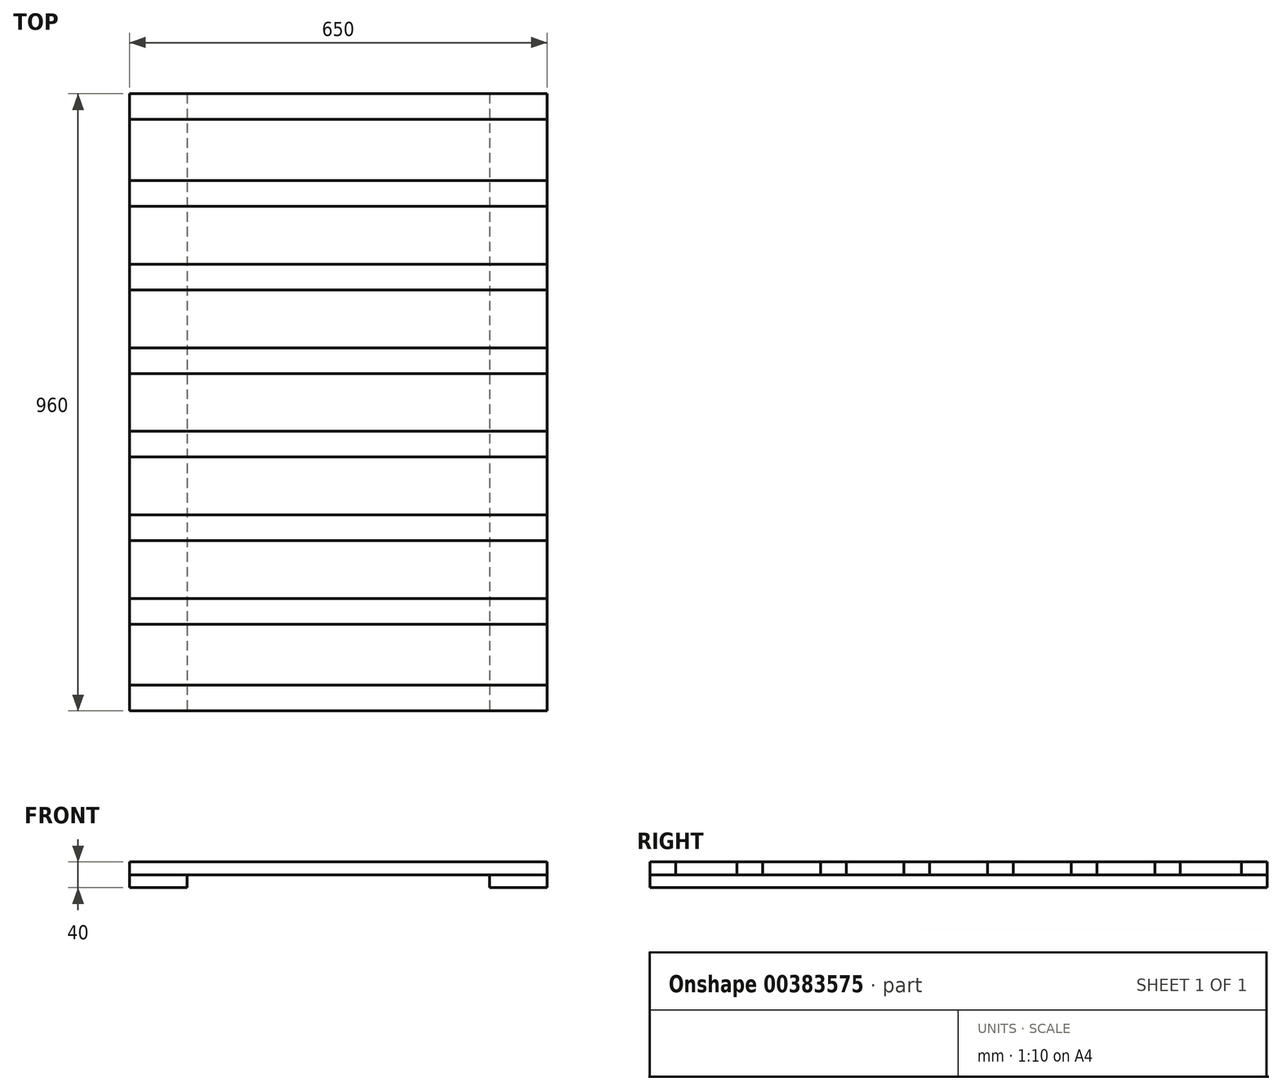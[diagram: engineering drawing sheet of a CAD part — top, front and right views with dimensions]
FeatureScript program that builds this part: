
annotation { "Feature Type Name" : "Feature", "Feature Type Description" : "" }
export const myFeature = defineFeature(function(context is Context, id is Id, definition is map)
    precondition{}
    {
        {
            var Q0;
            Q0=qCreatedBy(makeId("Top.planeOp"),FACE);
            var sketch = newSketch(context, id + "F0", { "sketchPlane" : qUnion([Q0])});
            skLineSegment(sketch, "E0.bottom", {"start": v(-273.15, 556.84) * mm, "end": v(376.85, 556.84) * mm});
            skLineSegment(sketch, "E0.top", {"start": v(-273.15, -403.16) * mm, "end": v(376.85, -403.16) * mm});
            skLineSegment(sketch, "E0.left", {"start": v(-273.15, 556.84) * mm, "end": v(-273.15, -403.16) * mm});
            skLineSegment(sketch, "E0.right", {"start": v(376.85, 556.84) * mm, "end": v(376.85, -403.16) * mm});
            skLineSegment(sketch, "E1", {"start": v(-273.15, 516.84) * mm, "end": v(376.85, 516.84) * mm});
            skLineSegment(sketch, "E2", {"start": v(-273.15, 421.84) * mm, "end": v(376.85, 421.84) * mm});
            skLineSegment(sketch, "E3", {"start": v(-273.15, 381.84) * mm, "end": v(376.85, 381.84) * mm});
            skLineSegment(sketch, "E4", {"start": v(-273.15, 291.84) * mm, "end": v(376.85, 291.84) * mm});
            skLineSegment(sketch, "E5", {"start": v(-273.15, 251.84) * mm, "end": v(376.85, 251.84) * mm});
            skLineSegment(sketch, "E6", {"start": v(-273.15, 161.84) * mm, "end": v(376.85, 161.84) * mm});
            skLineSegment(sketch, "E7", {"start": v(-273.15, 121.84) * mm, "end": v(376.85, 121.84) * mm});
            skLineSegment(sketch, "E8", {"start": v(-273.15, 31.84) * mm, "end": v(376.85, 31.84) * mm});
            skLineSegment(sketch, "E9", {"start": v(-273.15, -8.16) * mm, "end": v(376.85, -8.16) * mm});
            skLineSegment(sketch, "E10", {"start": v(-273.15, -98.16) * mm, "end": v(376.85, -98.16) * mm});
            skLineSegment(sketch, "E11", {"start": v(-273.15, -138.16) * mm, "end": v(376.85, -138.16) * mm});
            skLineSegment(sketch, "E12", {"start": v(-273.15, -228.16) * mm, "end": v(376.85, -228.16) * mm});
            skLineSegment(sketch, "E13", {"start": v(-273.15, -268.16) * mm, "end": v(376.85, -268.16) * mm});
            skLineSegment(sketch, "E14", {"start": v(-273.15, -363.16) * mm, "end": v(376.85, -363.16) * mm});
            skSolve(sketch);
        }
        {
            var Q0;
            {var subQ0=sQuery(id+"F0.wireOp",EDGE,"E0.bottom");Q0=makeQuery(id+"F0.imprint","IMPRINT",FACE,{"disambiguationData":[TD([[makeQuery(id+"F0.imprint","IMPRINT",EDGE,{"derivedFrom":subQ0}),-1.0]])]});}
            var Q1;
            {var subQ0=sQuery(id+"F0.wireOp",EDGE,"E2");Q1=makeQuery(id+"F0.imprint","IMPRINT",FACE,{"disambiguationData":[TD([[makeQuery(id+"F0.imprint","IMPRINT",EDGE,{"derivedFrom":subQ0}),-1.0]])]});}
            var Q2;
            {var subQ0=sQuery(id+"F0.wireOp",EDGE,"E4");Q2=makeQuery(id+"F0.imprint","IMPRINT",FACE,{"disambiguationData":[TD([[makeQuery(id+"F0.imprint","IMPRINT",EDGE,{"derivedFrom":subQ0}),-1.0]])]});}
            var Q3;
            {var subQ0=sQuery(id+"F0.wireOp",EDGE,"E6");Q3=makeQuery(id+"F0.imprint","IMPRINT",FACE,{"disambiguationData":[TD([[makeQuery(id+"F0.imprint","IMPRINT",EDGE,{"derivedFrom":subQ0}),-1.0]])]});}
            var Q4;
            {var subQ0=sQuery(id+"F0.wireOp",EDGE,"E8");Q4=makeQuery(id+"F0.imprint","IMPRINT",FACE,{"disambiguationData":[TD([[makeQuery(id+"F0.imprint","IMPRINT",EDGE,{"derivedFrom":subQ0}),-1.0]])]});}
            var Q5;
            {var subQ0=sQuery(id+"F0.wireOp",EDGE,"E10");Q5=makeQuery(id+"F0.imprint","IMPRINT",FACE,{"disambiguationData":[TD([[makeQuery(id+"F0.imprint","IMPRINT",EDGE,{"derivedFrom":subQ0}),-1.0]])]});}
            var Q6;
            {var subQ0=sQuery(id+"F0.wireOp",EDGE,"E12");Q6=makeQuery(id+"F0.imprint","IMPRINT",FACE,{"disambiguationData":[TD([[makeQuery(id+"F0.imprint","IMPRINT",EDGE,{"derivedFrom":subQ0}),-1.0]])]});}
            var Q7;
            {var subQ0=sQuery(id+"F0.wireOp",EDGE,"E0.top");Q7=makeQuery(id+"F0.imprint","IMPRINT",FACE,{"disambiguationData":[TD([[makeQuery(id+"F0.imprint","IMPRINT",EDGE,{"derivedFrom":subQ0}),1.0]])]});}
            extrude(context, id + "F1", {"entities" : qUnion([Q0, Q1, Q2, Q3, Q4, Q5, Q6, Q7]), "depth" : 20 * mm});
        }
        {
            var Q0;
            {var subQ0=sQuery(id+"F0.wireOp",EDGE,"E1");Q0=makeQuery(id+"F0.imprint","IMPRINT",FACE,{"disambiguationData":[TD([[makeQuery(id+"F0.imprint","IMPRINT",EDGE,{"derivedFrom":subQ0}),-1.0]])]});}
            var Q1;
            {var subQ0=sQuery(id+"F0.wireOp",EDGE,"E3");Q1=makeQuery(id+"F0.imprint","IMPRINT",FACE,{"disambiguationData":[TD([[makeQuery(id+"F0.imprint","IMPRINT",EDGE,{"derivedFrom":subQ0}),-1.0]])]});}
            var Q2;
            {var subQ0=sQuery(id+"F0.wireOp",EDGE,"E5");Q2=makeQuery(id+"F0.imprint","IMPRINT",FACE,{"disambiguationData":[TD([[makeQuery(id+"F0.imprint","IMPRINT",EDGE,{"derivedFrom":subQ0}),-1.0]])]});}
            var Q3;
            {var subQ0=sQuery(id+"F0.wireOp",EDGE,"E7");Q3=makeQuery(id+"F0.imprint","IMPRINT",FACE,{"disambiguationData":[TD([[makeQuery(id+"F0.imprint","IMPRINT",EDGE,{"derivedFrom":subQ0}),-1.0]])]});}
            var Q4;
            {var subQ0=sQuery(id+"F0.wireOp",EDGE,"E9");Q4=makeQuery(id+"F0.imprint","IMPRINT",FACE,{"disambiguationData":[TD([[makeQuery(id+"F0.imprint","IMPRINT",EDGE,{"derivedFrom":subQ0}),-1.0]])]});}
            var Q5;
            {var subQ0=sQuery(id+"F0.wireOp",EDGE,"E11");Q5=makeQuery(id+"F0.imprint","IMPRINT",FACE,{"disambiguationData":[TD([[makeQuery(id+"F0.imprint","IMPRINT",EDGE,{"derivedFrom":subQ0}),-1.0]])]});}
            var Q6;
            {var subQ0=sQuery(id+"F0.wireOp",EDGE,"E13");Q6=makeQuery(id+"F0.imprint","IMPRINT",FACE,{"disambiguationData":[TD([[makeQuery(id+"F0.imprint","IMPRINT",EDGE,{"derivedFrom":subQ0}),-1.0]])]});}
            extrude(context, id + "F2", {"entities" : qUnion([Q0, Q1, Q2, Q3, Q4, Q5, Q6]), "depth" : 20 * mm});
        }
        {
            var Q0;
            Q0=makeQuery(id+"F2.opExtrude","CAP_FACE",FACE,{"disambiguationData":[OSD([sQuery(id+"F0.wireOp",EDGE,"E0.left"),sQuery(id+"F0.wireOp",EDGE,"E0.right"),sQuery(id+"F0.wireOp",EDGE,"E3"),sQuery(id+"F0.wireOp",EDGE,"E4")])],"isStart":true});
            var sketch = newSketch(context, id + "F3", { "sketchPlane" : qUnion([Q0])});
            skLineSegment(sketch, "E15.bottom", {"start": v(376.85, -556.84) * mm, "end": v(286.85, -556.84) * mm});
            skLineSegment(sketch, "E15.top", {"start": v(376.85, 403.16) * mm, "end": v(286.85, 403.16) * mm});
            skLineSegment(sketch, "E15.left", {"start": v(376.85, -556.84) * mm, "end": v(376.85, 403.16) * mm});
            skLineSegment(sketch, "E15.right", {"start": v(286.85, -556.84) * mm, "end": v(286.85, 403.16) * mm});
            skLineSegment(sketch, "E16.bottom", {"start": v(-183.15, -556.84) * mm, "end": v(-273.15, -556.84) * mm});
            skLineSegment(sketch, "E16.top", {"start": v(-183.15, 403.16) * mm, "end": v(-273.15, 403.16) * mm});
            skLineSegment(sketch, "E16.left", {"start": v(-183.15, -556.84) * mm, "end": v(-183.15, 403.16) * mm});
            skLineSegment(sketch, "E16.right", {"start": v(-273.15, -556.84) * mm, "end": v(-273.15, 403.16) * mm});
            skSolve(sketch);
        }
        {
            var Q0;
            {var subQ0=sQuery(id+"F3.wireOp",EDGE,"E15.bottom");Q0=makeQuery(id+"F3.imprint","IMPRINT",FACE,{"disambiguationData":[TD([[makeQuery(id+"F3.imprint","IMPRINT",EDGE,{"derivedFrom":subQ0}),-1.0]])]});}
            var Q1;
            {var subQ0=sQuery(id+"F3.wireOp",EDGE,"E15.left");var subQ1=makeQuery(id+"F2.opExtrude","CAP_EDGE",EDGE,{"disambiguationData":[OSD([sQuery(id+"F0.wireOp",EDGE,"E3")])],"isStart":true});var subQ2=makeQuery(id+"F3.imprint","INTERSECT",VERTEX,{"derivedFrom":[subQ1,subQ0]});Q1=makeQuery(id+"F3.imprint","IMPRINT",FACE,{"disambiguationData":[TD([[makeQuery(id+"F3.imprint","IMPRINT",EDGE,{"disambiguationData":[TD([[subQ2,-1.0]])],"derivedFrom":subQ0}),1.0]])]});}
            var Q2;
            {var subQ0=sQuery(id+"F3.wireOp",EDGE,"E15.top");Q2=makeQuery(id+"F3.imprint","IMPRINT",FACE,{"disambiguationData":[TD([[makeQuery(id+"F3.imprint","IMPRINT",EDGE,{"derivedFrom":subQ0}),1.0]])]});}
            var Q3;
            {var subQ0=sQuery(id+"F3.wireOp",EDGE,"E16.top");Q3=makeQuery(id+"F3.imprint","IMPRINT",FACE,{"disambiguationData":[TD([[makeQuery(id+"F3.imprint","IMPRINT",EDGE,{"derivedFrom":subQ0}),1.0]])]});}
            var Q4;
            {var subQ0=sQuery(id+"F3.wireOp",EDGE,"E16.left");var subQ1=makeQuery(id+"F2.opExtrude","CAP_EDGE",EDGE,{"disambiguationData":[OSD([sQuery(id+"F0.wireOp",EDGE,"E3")])],"isStart":true});var subQ2=makeQuery(id+"F3.imprint","INTERSECT",VERTEX,{"derivedFrom":[subQ1,subQ0]});Q4=makeQuery(id+"F3.imprint","IMPRINT",FACE,{"disambiguationData":[TD([[makeQuery(id+"F3.imprint","IMPRINT",EDGE,{"disambiguationData":[TD([[subQ2,-1.0]])],"derivedFrom":subQ0}),1.0]])]});}
            var Q5;
            {var subQ0=sQuery(id+"F3.wireOp",EDGE,"E16.bottom");Q5=makeQuery(id+"F3.imprint","IMPRINT",FACE,{"disambiguationData":[TD([[makeQuery(id+"F3.imprint","IMPRINT",EDGE,{"derivedFrom":subQ0}),-1.0]])]});}
            extrude(context, id + "F4", {"entities" : qUnion([Q0, Q1, Q2, Q3, Q4, Q5]), "depth" : 20 * mm});
        }
    });
